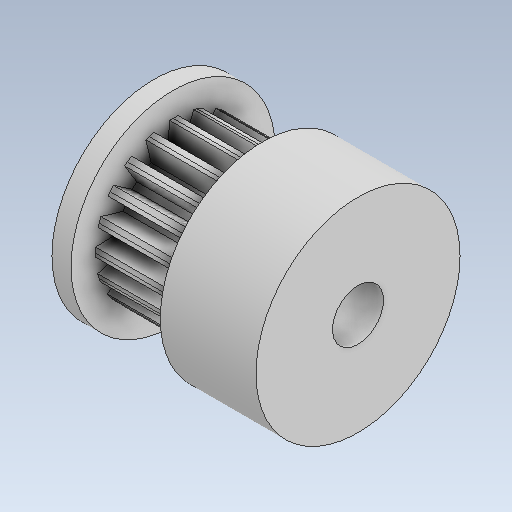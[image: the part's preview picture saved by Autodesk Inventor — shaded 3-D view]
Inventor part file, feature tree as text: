
AUTODESK INVENTOR PART (.ipt)
format: ipt  version: 2020 (Build 240168000, 168)  size: 283,648 bytes
history: native  units: mm
features: extrude x5, sketch x3, projected_geometry x2, other x1
ambient origin geometry x8: Origin, YZ Plane, XZ Plane, XY Plane, X Axis, Y Axis, Z Axis, Center Point
bodies: Body1 (feature_tree)
feature tree (11):
  other  "Твердое тело1"
  extrude  "Выдавливание1"  Depth=12.2mm
  extrude  "Выдавливание2"  Depth=7.0mm TaperAngle=0.0deg
  extrude  "Выдавливание3"  Depth=16.0mm
  extrude  "Выдавливание4"  Depth=7.5mm TaperAngle=0.0deg
  extrude  "Выдавливание5"  Depth=16.0mm
  sketch  "Эскиз1"
  sketch  "Эскиз2"
  sketch  "Эскиз4"
  projected_geometry  "Спроецированная петля1"
  projected_geometry  "Спроецированная петля2"
